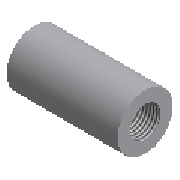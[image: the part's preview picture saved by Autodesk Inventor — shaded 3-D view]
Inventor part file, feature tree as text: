
AUTODESK INVENTOR PART (.ipt)
format: ipt  version: 2023 (Build 270158000, 158)  size: 161,280 bytes
history: native  units: mm (DEFAULTED — no unit token found)
features: other x6, thread x2, sketch x1, revolve x1
ambient origin geometry x8: Origin, YZ Plane, XZ Plane, XY Plane, X Axis, Y Axis, Z Axis, Center Point
bodies: Solid1 (feature_tree)
feature tree (10):
  sketch  "Sketch1"  dims[d6=90.0deg d0=8.736838mm d1=31.75mm d2=15.748mm d16=25.4mm d17=0.0mm d18=25.4mm d19=0.0mm d3=0.312398mm d4=6.70306mm]
  revolve  "Revolve1"  [1 undecoded]
  thread  "Thread1"  [1 undecoded]
  thread  "Thread2"  [1 undecoded]
  other  "Work Point1"
  other  "Work Point2"
  other  "Work Axis1"
  other  "Work Point3"
  other  "Work Axis2"
  other  "Work Point4"
note: 3 required parameter values undecoded (feature->parameter linkage not recoverable at this tier; creation-order binding heuristic only, values carry confidence <= 0.55)